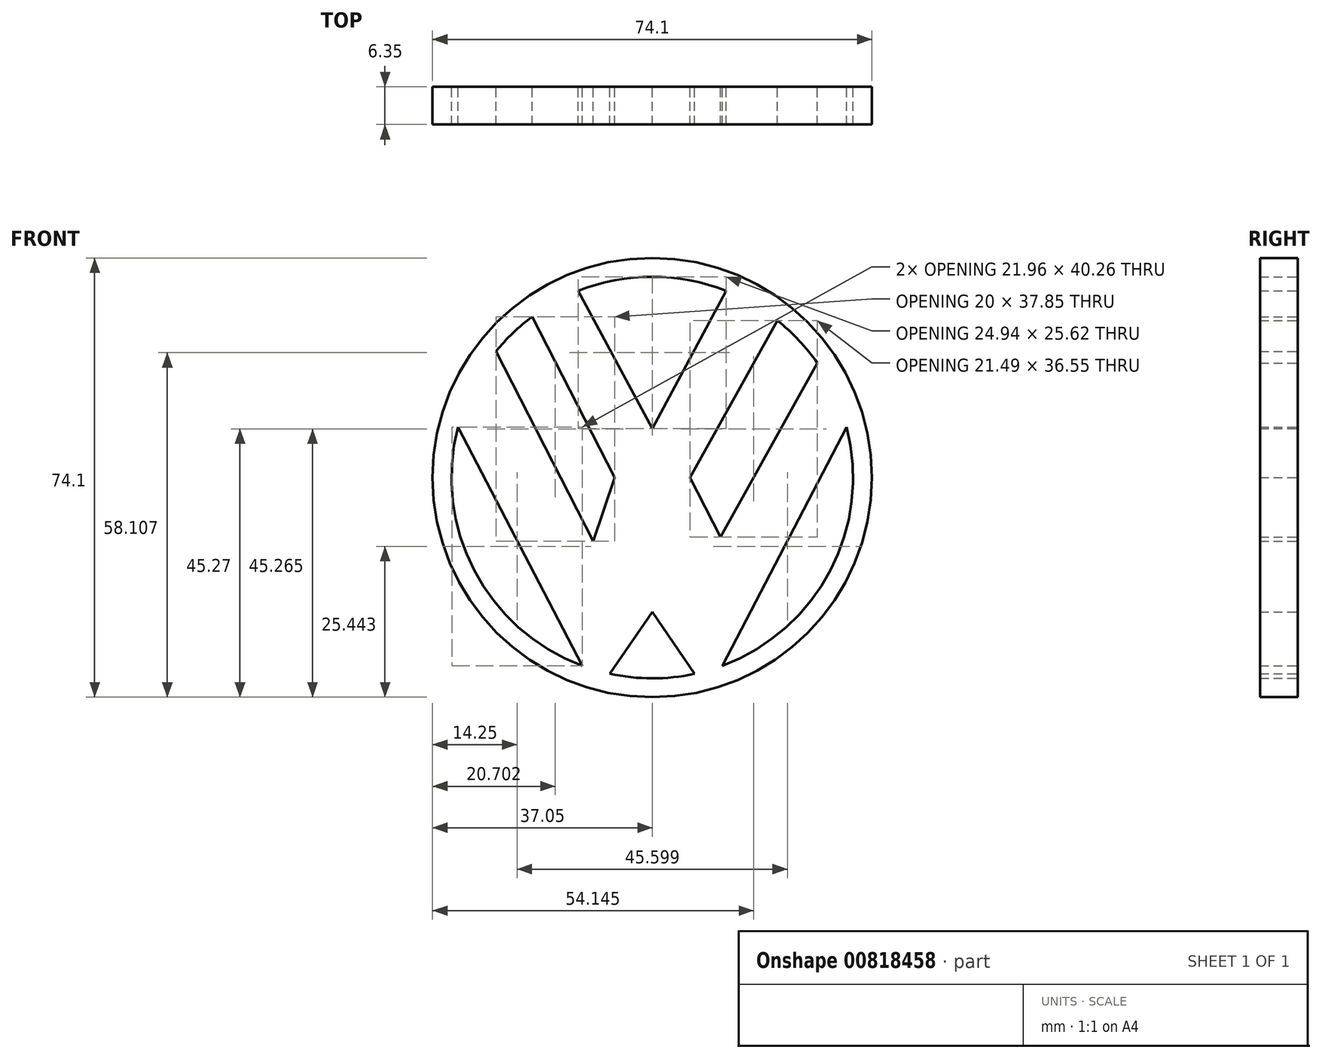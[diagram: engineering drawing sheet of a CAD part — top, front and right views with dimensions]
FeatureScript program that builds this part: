
annotation { "Feature Type Name" : "Feature", "Feature Type Description" : "" }
export const myFeature = defineFeature(function(context is Context, id is Id, definition is map)
    precondition{}
    {
        {
            var Q0;
            Q0=qCreatedBy(makeId("Front.planeOp"),FACE);
            var sketch = newSketch(context, id + "F0", { "sketchPlane" : qUnion([Q0])});
            skCircle(sketch, "E0", {"center": v(0, 0) * mm, "radius": 37.05 * mm});
            skCircle(sketch, "E1", {"center": v(0, 0) * mm, "radius": 33.86 * mm});
            skLineSegment(sketch, "E2", {"start": v(0, 33.86) * mm, "end": v(0, -33.86) * mm, "construction": true});
            skLineSegment(sketch, "E3", {"start": v(-6.35, 0) * mm, "end": v(-20.25, 27.14) * mm});
            skLineSegment(sketch, "E4", {"start": v(6.35, 0) * mm, "end": v(21.1, 26.49) * mm});
            skLineSegment(sketch, "E5", {"start": v(-6.35, 0) * mm, "end": v(6.35, 0) * mm});
            skLineSegment(sketch, "E6", {"start": v(-6.35, 0) * mm, "end": v(-9.97, -10.7) * mm});
            skLineSegment(sketch, "E7", {"start": v(-9.97, -10.7) * mm, "end": v(-26.35, 21.28) * mm});
            skLineSegment(sketch, "E8", {"start": v(6.35, 0) * mm, "end": v(11.5, -10.06) * mm});
            skLineSegment(sketch, "E9", {"start": v(11.5, -10.06) * mm, "end": v(27.84, 19.28) * mm});
            skLineSegment(sketch, "E10", {"start": v(-32.78, 8.52) * mm, "end": v(-11.82, -31.74) * mm});
            skLineSegment(sketch, "E11", {"start": v(11.82, -31.74) * mm, "end": v(32.78, 8.52) * mm});
            skLineSegment(sketch, "E12", {"start": v(-12.47, 31.48) * mm, "end": v(0, 8.25) * mm});
            skLineSegment(sketch, "E13", {"start": v(0, 8.25) * mm, "end": v(12.47, 31.48) * mm});
            skCircle(sketch, "E14", {"center": v(0, 0) * mm, "radius": 48.2 * mm});
            skLineSegment(sketch, "E15", {"start": v(-7.2, -33.1) * mm, "end": v(0, -22.66) * mm});
            skLineSegment(sketch, "E16", {"start": v(0, -22.66) * mm, "end": v(7.12, -33.1) * mm});
            skSolve(sketch);
        }
        {
            var Q0;
            Q0=makeQuery(id+"F0.imprint","IMPRINT",FACE,{"disambiguationData":[TD([[makeQuery(id+"F0.imprint","IMPRINT",EDGE,{"derivedFrom":sQuery(id+"F0.wireOp",EDGE,"E0")}),1.0]])]});
            var Q1;
            Q1=makeQuery(id+"F0.imprint","IMPRINT",FACE,{"disambiguationData":[TD([[makeQuery(id+"F0.imprint","IMPRINT",EDGE,{"derivedFrom":sQuery(id+"F0.wireOp",EDGE,"E5")}),-1.0]])]});
            var Q2;
            {var subQ3=sQuery(id+"F0.wireOp",EDGE,"E3");Q2=makeQuery(id+"F0.imprint","IMPRINT",FACE,{"disambiguationData":[TD([[makeQuery(id+"F0.imprint","IMPRINT",EDGE,{"derivedFrom":subQ3}),-1.0]])]});}
            extrude(context, id + "F1", {"entities" : qUnion([Q0, Q1, Q2]), "depth" : 6.35 * mm, "offsetDistance" : 25.4 * mm});
        }
    });
